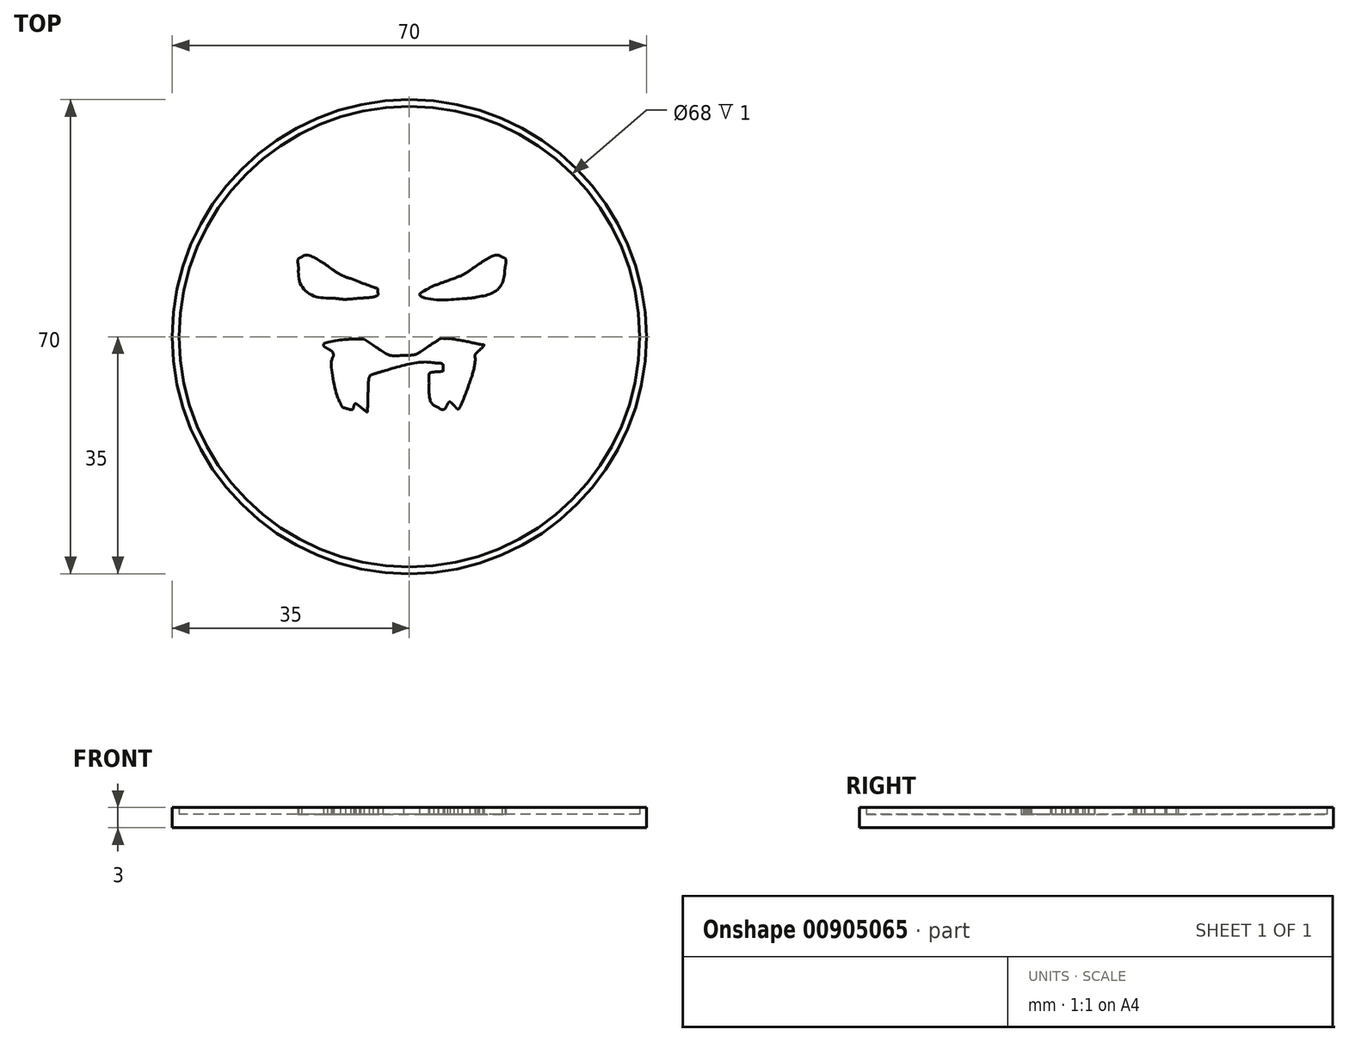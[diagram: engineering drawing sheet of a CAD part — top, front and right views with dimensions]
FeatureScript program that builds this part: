
annotation { "Feature Type Name" : "Feature", "Feature Type Description" : "" }
export const myFeature = defineFeature(function(context is Context, id is Id, definition is map)
    precondition{}
    {
        {
            var Q0;
            Q0=qCreatedBy(makeId("Top.planeOp"),FACE);
            var sketch = newSketch(context, id + "F0", { "sketchPlane" : qUnion([Q0])});
            skLineSegment(sketch, "E0", {"start": v(16.84, 6.63) * mm, "end": v(16.18, 5.27) * mm});
            skLineSegment(sketch, "E1", {"start": v(16.18, 5.27) * mm, "end": v(16.32, 4.06) * mm});
            skLineSegment(sketch, "E2", {"start": v(16.47, -0.82) * mm, "end": v(15.75, -0.73) * mm});
            skLineSegment(sketch, "E3", {"start": v(15.75, -0.73) * mm, "end": v(15.82, -1.4) * mm});
            skLineSegment(sketch, "E4", {"start": v(15.72, -10.07) * mm, "end": v(14.53, -10.08) * mm});
            skLineSegment(sketch, "E5", {"start": v(14.53, -10.08) * mm, "end": v(14.58, -11.4) * mm});
            skLineSegment(sketch, "E6", {"start": v(12.3, -13.5) * mm, "end": v(11.89, -13) * mm});
            skLineSegment(sketch, "E7", {"start": v(11.89, -13) * mm, "end": v(11.47, -13.22) * mm});
            skLineSegment(sketch, "E8", {"start": v(-5.34, 5.77) * mm, "end": v(-6.7, 6.68) * mm});
            skLineSegment(sketch, "E9", {"start": v(-6.7, 6.68) * mm, "end": v(-7.9, 6.65) * mm});
            skFitSpline(sketch, "E10", {"points": [v(0.33, -24.03) * mm, v(-0.4, -23.24) * mm, v(-1.2, -21.92) * mm, v(-1.9, -20.3) * mm]});
            skFitSpline(sketch, "E11", {"points": [v(-1.9, -20.3) * mm, v(-2.2, -19.61) * mm, v(-2.49, -19) * mm, v(-2.55, -18.93) * mm]});
            skFitSpline(sketch, "E12", {"points": [v(-2.55, -18.93) * mm, v(-2.61, -18.87) * mm, v(-2.73, -19.07) * mm, v(-2.8, -19.4) * mm]});
            skFitSpline(sketch, "E13", {"points": [v(-2.8, -19.4) * mm, v(-3.12, -20.6) * mm, v(-3.98, -22.41) * mm, v(-4.25, -22.41) * mm]});
            skFitSpline(sketch, "E14", {"points": [v(-4.25, -22.41) * mm, v(-4.3, -22.41) * mm, v(-4.47, -22.16) * mm, v(-4.6, -21.85) * mm]});
            skFitSpline(sketch, "E15", {"points": [v(-4.6, -21.85) * mm, v(-5.08, -20.8) * mm, v(-7.45, -18.8) * mm, v(-9.5, -17.73) * mm]});
            skFitSpline(sketch, "E16", {"points": [v(-9.5, -17.73) * mm, v(-10.12, -17.41) * mm, v(-10.24, -17.4) * mm, v(-10.66, -17.53) * mm]});
            skFitSpline(sketch, "E17", {"points": [v(-10.66, -17.53) * mm, v(-10.93, -17.62) * mm, v(-11.34, -17.94) * mm, v(-11.65, -18.3) * mm]});
            skFitSpline(sketch, "E18", {"points": [v(-11.65, -18.3) * mm, v(-12.3, -19.05) * mm, v(-12.42, -18.97) * mm, v(-12.62, -17.67) * mm]});
            skFitSpline(sketch, "E19", {"points": [v(-12.62, -17.67) * mm, v(-12.78, -16.65) * mm, v(-12.7, -16.7) * mm, v(-13.62, -16.96) * mm]});
            skFitSpline(sketch, "E20", {"points": [v(-13.62, -16.96) * mm, v(-13.9, -17.04) * mm, v(-13.93, -17.01) * mm, v(-13.84, -16.73) * mm]});
            skFitSpline(sketch, "E21", {"points": [v(-13.84, -16.73) * mm, v(-13.56, -15.8) * mm, v(-13.53, -15.46) * mm, v(-13.65, -14.74) * mm]});
            skFitSpline(sketch, "E22", {"points": [v(-13.65, -14.74) * mm, v(-13.79, -13.85) * mm, v(-14.24, -12.57) * mm, v(-14.45, -12.43) * mm]});
            skFitSpline(sketch, "E23", {"points": [v(-14.45, -12.43) * mm, v(-14.53, -12.38) * mm, v(-14.7, -12.46) * mm, v(-14.8, -12.6) * mm]});
            skFitSpline(sketch, "E24", {"points": [v(-14.8, -12.6) * mm, v(-15.1, -12.95) * mm, v(-15.63, -13.3) * mm, v(-15.87, -13.3) * mm]});
            skFitSpline(sketch, "E25", {"points": [v(-15.87, -13.3) * mm, v(-16.05, -13.3) * mm, v(-16.08, -12.94) * mm, v(-16.09, -10.64) * mm]});
            skFitSpline(sketch, "E26", {"points": [v(-16.09, -10.64) * mm, v(-16.1, -9.17) * mm, v(-16.16, -7.82) * mm, v(-16.23, -7.64) * mm]});
            skFitSpline(sketch, "E27", {"points": [v(-16.23, -7.64) * mm, v(-16.36, -7.33) * mm, v(-16.39, -7.32) * mm, v(-17.7, -7.36) * mm]});
            skFitSpline(sketch, "E28", {"points": [v(-17.7, -7.36) * mm, v(-19.04, -7.4) * mm, v(-19.26, -7.32) * mm, v(-18.83, -6.97) * mm]});
            skFitSpline(sketch, "E29", {"points": [v(-18.83, -6.97) * mm, v(-18.49, -6.68) * mm, v(-17.98, -5.55) * mm, v(-17.75, -4.55) * mm]});
            skFitSpline(sketch, "E30", {"points": [v(-17.75, -4.55) * mm, v(-17.45, -3.23) * mm, v(-17.46, 0.97) * mm, v(-17.77, 3.12) * mm]});
            skFitSpline(sketch, "E31", {"points": [v(-17.77, 3.12) * mm, v(-17.98, 4.54) * mm, v(-18.06, 4.8) * mm, v(-18.59, 5.71) * mm]});
            skFitSpline(sketch, "E32", {"points": [v(-18.59, 5.71) * mm, v(-19.63, 7.52) * mm, v(-20.1, 8.95) * mm, v(-20.1, 10.3) * mm]});
            skFitSpline(sketch, "E33", {"points": [v(-20.1, 10.3) * mm, v(-20.1, 11.28) * mm, v(-19.85, 11.91) * mm, v(-19.13, 12.85) * mm]});
            skFitSpline(sketch, "E34", {"points": [v(-19.13, 12.85) * mm, v(-18.32, 13.92) * mm, v(-18.18, 15.6) * mm, v(-18.78, 17.2) * mm]});
            skFitSpline(sketch, "E35", {"points": [v(-18.78, 17.2) * mm, v(-18.94, 17.63) * mm, v(-19.36, 18.28) * mm, v(-19.83, 18.83) * mm]});
            skFitSpline(sketch, "E36", {"points": [v(-19.83, 18.83) * mm, v(-20.73, 19.86) * mm, v(-21.42, 21.09) * mm, v(-21.75, 22.23) * mm]});
            skFitSpline(sketch, "E37", {"points": [v(-21.75, 22.23) * mm, v(-22.09, 23.4) * mm, v(-21.97, 26.07) * mm, v(-21.5, 27.62) * mm]});
            skFitSpline(sketch, "E38", {"points": [v(-21.5, 27.62) * mm, v(-21.06, 29.09) * mm, v(-19.85, 31.81) * mm, v(-19.64, 31.81) * mm]});
            skFitSpline(sketch, "E39", {"points": [v(-19.64, 31.81) * mm, v(-19.03, 31.81) * mm, v(-17.7, 30.26) * mm, v(-17.45, 29.24) * mm]});
            skFitSpline(sketch, "E40", {"points": [v(-17.45, 29.24) * mm, v(-17.06, 27.73) * mm, v(-16.88, 27.3) * mm, v(-16.29, 26.4) * mm]});
            skFitSpline(sketch, "E41", {"points": [v(-16.29, 26.4) * mm, v(-15.47, 25.16) * mm, v(-13.78, 23.52) * mm, v(-12.83, 23.06) * mm]});
            skFitSpline(sketch, "E42", {"points": [v(-12.83, 23.06) * mm, v(-12.39, 22.84) * mm, v(-11.72, 22.66) * mm, v(-11.06, 22.58) * mm]});
            skFitSpline(sketch, "E43", {"points": [v(-11.06, 22.58) * mm, v(-10.19, 22.47) * mm, v(-9.75, 22.33) * mm, v(-8.55, 21.72) * mm]});
            skFitSpline(sketch, "E44", {"points": [v(-8.55, 21.72) * mm, v(-7.76, 21.32) * mm, v(-6.36, 20.46) * mm, v(-5.45, 19.81) * mm]});
            skFitSpline(sketch, "E45", {"points": [v(-5.45, 19.81) * mm, v(-2.3, 17.56) * mm, v(-1.48, 17.03) * mm, v(-1.14, 17.03) * mm]});
            skFitSpline(sketch, "E46", {"points": [v(-1.14, 17.03) * mm, v(-0.74, 17.03) * mm, v(0.04, 17.5) * mm, v(1.7, 18.72) * mm]});
            skFitSpline(sketch, "E47", {"points": [v(1.7, 18.72) * mm, v(5.41, 21.46) * mm, v(7.07, 22.35) * mm, v(8.88, 22.58) * mm]});
            skFitSpline(sketch, "E48", {"points": [v(8.88, 22.58) * mm, v(9.43, 22.65) * mm, v(10.18, 22.85) * mm, v(10.6, 23.05) * mm]});
            skFitSpline(sketch, "E49", {"points": [v(10.6, 23.05) * mm, v(12.39, 23.9) * mm, v(14.82, 26.94) * mm, v(15.07, 28.67) * mm]});
            skFitSpline(sketch, "E50", {"points": [v(15.07, 28.67) * mm, v(15.26, 29.87) * mm, v(16.74, 31.9) * mm, v(17.36, 31.78) * mm]});
            skFitSpline(sketch, "E51", {"points": [v(17.36, 31.78) * mm, v(17.77, 31.7) * mm, v(19.17, 28.33) * mm, v(19.55, 26.5) * mm]});
            skFitSpline(sketch, "E52", {"points": [v(19.55, 26.5) * mm, v(19.8, 25.32) * mm, v(19.8, 23.23) * mm, v(19.55, 22.27) * mm]});
            skFitSpline(sketch, "E53", {"points": [v(19.55, 22.27) * mm, v(19.26, 21.16) * mm, v(18.67, 20.08) * mm, v(17.75, 18.99) * mm]});
            skFitSpline(sketch, "E54", {"points": [v(17.75, 18.99) * mm, v(16.83, 17.9) * mm, v(16.6, 17.5) * mm, v(16.36, 16.57) * mm]});
            skFitSpline(sketch, "E55", {"points": [v(16.36, 16.57) * mm, v(16, 15.18) * mm, v(16.24, 13.67) * mm, v(17, 12.73) * mm]});
            skFitSpline(sketch, "E56", {"points": [v(17, 12.73) * mm, v(18.26, 11.16) * mm, v(18.22, 9.49) * mm, v(16.84, 6.63) * mm]});
            skFitSpline(sketch, "E57", {"points": [v(16.32, 4.06) * mm, v(16.54, 2.03) * mm, v(16.85, 0.43) * mm, v(17.17, -0.32) * mm]});
            skFitSpline(sketch, "E58", {"points": [v(17.17, -0.32) * mm, v(17.27, -0.56) * mm, v(17.31, -0.79) * mm, v(17.27, -0.83) * mm]});
            skFitSpline(sketch, "E59", {"points": [v(17.27, -0.83) * mm, v(17.23, -0.87) * mm, v(16.87, -0.87) * mm, v(16.47, -0.82) * mm]});
            skFitSpline(sketch, "E60", {"points": [v(15.82, -1.4) * mm, v(15.93, -2.32) * mm, v(16.3, -2.98) * mm, v(17.38, -4.21) * mm]});
            skFitSpline(sketch, "E61", {"points": [v(17.38, -4.21) * mm, v(18.3, -5.26) * mm, v(18.3, -5.26) * mm, v(17.99, -5.4) * mm]});
            skFitSpline(sketch, "E62", {"points": [v(17.99, -5.4) * mm, v(17.74, -5.52) * mm, v(17.5, -5.5) * mm, v(16.96, -5.35) * mm]});
            skFitSpline(sketch, "E63", {"points": [v(16.96, -5.35) * mm, v(16.57, -5.23) * mm, v(16.2, -5.19) * mm, v(16.15, -5.24) * mm]});
            skFitSpline(sketch, "E64", {"points": [v(16.15, -5.24) * mm, v(15.8, -5.6) * mm, v(16.77, -7.73) * mm, v(17.73, -8.72) * mm]});
            skFitSpline(sketch, "E65", {"points": [v(17.73, -8.72) * mm, v(18.15, -9.15) * mm, v(18.18, -9.23) * mm, v(18.02, -9.43) * mm]});
            skFitSpline(sketch, "E66", {"points": [v(18.02, -9.43) * mm, v(17.67, -9.85) * mm, v(16.95, -10.05) * mm, v(15.72, -10.07) * mm]});
            skFitSpline(sketch, "E67", {"points": [v(14.58, -11.4) * mm, v(14.6, -12.3) * mm, v(14.56, -12.97) * mm, v(14.42, -13.52) * mm]});
            skFitSpline(sketch, "E68", {"points": [v(14.42, -13.52) * mm, v(14.18, -14.43) * mm, v(13.68, -15.68) * mm, v(13.56, -15.68) * mm]});
            skFitSpline(sketch, "E69", {"points": [v(13.56, -15.68) * mm, v(13.5, -15.68) * mm, v(13.3, -15.3) * mm, v(13.1, -14.84) * mm]});
            skFitSpline(sketch, "E70", {"points": [v(13.1, -14.84) * mm, v(12.9, -14.37) * mm, v(12.54, -13.77) * mm, v(12.3, -13.5) * mm]});
            skFitSpline(sketch, "E71", {"points": [v(11.47, -13.22) * mm, v(10.74, -13.6) * mm, v(9.51, -14.85) * mm, v(9.1, -15.64) * mm]});
            skFitSpline(sketch, "E72", {"points": [v(9.1, -15.64) * mm, v(8.87, -16.07) * mm, v(8.56, -16.91) * mm, v(8.4, -17.53) * mm]});
            skFitSpline(sketch, "E73", {"points": [v(8.4, -17.53) * mm, v(8.05, -19) * mm, v(7.59, -19.88) * mm, v(6.68, -20.86) * mm]});
            skFitSpline(sketch, "E74", {"points": [v(6.68, -20.86) * mm, v(5.89, -21.73) * mm, v(5.63, -21.77) * mm, v(5.63, -21.04) * mm]});
            skFitSpline(sketch, "E75", {"points": [v(5.63, -21.04) * mm, v(5.63, -20.56) * mm, v(4.88, -18.96) * mm, v(4.44, -18.49) * mm]});
            skFitSpline(sketch, "E76", {"points": [v(4.44, -18.49) * mm, v(4.22, -18.24) * mm, v(4.11, -18.21) * mm, v(3.9, -18.33) * mm]});
            skFitSpline(sketch, "E77", {"points": [v(3.9, -18.33) * mm, v(3.17, -18.72) * mm, v(2.35, -20.5) * mm, v(1.7, -23.1) * mm]});
            skFitSpline(sketch, "E78", {"points": [v(1.7, -23.1) * mm, v(1.44, -24.09) * mm, v(1.25, -24.6) * mm, v(1.12, -24.63) * mm]});
            skFitSpline(sketch, "E79", {"points": [v(1.12, -24.63) * mm, v(1.01, -24.65) * mm, v(0.66, -24.38) * mm, v(0.33, -24.03) * mm]});
            skFitSpline(sketch, "E80", {"points": [v(-6.1, -1.5) * mm, v(-6.06, -0.27) * mm, v(-5.98, 0.84) * mm, v(-5.92, 0.96) * mm]});
            skFitSpline(sketch, "E81", {"points": [v(-5.92, 0.96) * mm, v(-5.8, 1.25) * mm, v(-5.24, 1.51) * mm, v(-3.87, 1.9) * mm]});
            skFitSpline(sketch, "E82", {"points": [v(-3.87, 1.9) * mm, v(-0.9, 2.77) * mm, v(2.08, 3.26) * mm, v(3.62, 3.14) * mm]});
            skFitSpline(sketch, "E83", {"points": [v(3.62, 3.14) * mm, v(4.74, 3.06) * mm, v(4.97, 2.92) * mm, v(4.97, 2.33) * mm]});
            skFitSpline(sketch, "E84", {"points": [v(4.97, 2.33) * mm, v(4.97, 1.9) * mm, v(4.96, 1.9) * mm, v(4.22, 1.82) * mm]});
            skFitSpline(sketch, "E85", {"points": [v(4.22, 1.82) * mm, v(3.12, 1.7) * mm, v(2.92, 1.46) * mm, v(2.93, 0.18) * mm]});
            skFitSpline(sketch, "E86", {"points": [v(2.93, 0.18) * mm, v(2.95, -1.77) * mm, v(3.39, -2.93) * mm, v(4.29, -3.46) * mm]});
            skFitSpline(sketch, "E87", {"points": [v(4.29, -3.46) * mm, v(4.82, -3.77) * mm, v(5.26, -3.62) * mm, v(5.6, -3.02) * mm]});
            skFitSpline(sketch, "E88", {"points": [v(5.6, -3.02) * mm, v(5.73, -2.8) * mm, v(5.9, -2.62) * mm, v(5.98, -2.62) * mm]});
            skFitSpline(sketch, "E89", {"points": [v(5.98, -2.62) * mm, v(6.06, -2.62) * mm, v(6.34, -2.86) * mm, v(6.6, -3.15) * mm]});
            skFitSpline(sketch, "E90", {"points": [v(6.6, -3.15) * mm, v(6.86, -3.44) * mm, v(7.12, -3.68) * mm, v(7.18, -3.68) * mm]});
            skFitSpline(sketch, "E91", {"points": [v(7.18, -3.68) * mm, v(7.29, -3.68) * mm, v(8.5, -0.89) * mm, v(8.94, 0.37) * mm]});
            skFitSpline(sketch, "E92", {"points": [v(8.94, 0.37) * mm, v(9.3, 1.41) * mm, v(9.71, 3.27) * mm, v(9.72, 3.9) * mm]});
            skFitSpline(sketch, "E93", {"points": [v(9.72, 3.9) * mm, v(9.72, 4.34) * mm, v(9.8, 4.5) * mm, v(10.31, 4.98) * mm]});
            skFitSpline(sketch, "E94", {"points": [v(10.31, 4.98) * mm, v(10.86, 5.51) * mm, v(11.05, 5.82) * mm, v(10.8, 5.82) * mm]});
            skFitSpline(sketch, "E95", {"points": [v(10.8, 5.82) * mm, v(10.75, 5.82) * mm, v(10.26, 5.91) * mm, v(9.72, 6.03) * mm]});
            skFitSpline(sketch, "E96", {"points": [v(9.72, 6.03) * mm, v(7.88, 6.42) * mm, v(5.83, 6.74) * mm, v(5.21, 6.74) * mm]});
            skFitSpline(sketch, "E97", {"points": [v(5.21, 6.74) * mm, v(4.69, 6.74) * mm, v(4.43, 6.63) * mm, v(3.37, 5.93) * mm]});
            skFitSpline(sketch, "E98", {"points": [v(3.37, 5.93) * mm, v(1.35, 4.6) * mm, v(0.64, 4.32) * mm, v(-0.84, 4.26) * mm]});
            skFitSpline(sketch, "E99", {"points": [v(-0.84, 4.26) * mm, v(-2.49, 4.2) * mm, v(-3.46, 4.52) * mm, v(-5.34, 5.77) * mm]});
            skFitSpline(sketch, "E100", {"points": [v(-7.9, 6.65) * mm, v(-9.17, 6.62) * mm, v(-12.6, 5.97) * mm, v(-12.66, 5.75) * mm]});
            skFitSpline(sketch, "E101", {"points": [v(-12.66, 5.75) * mm, v(-12.68, 5.68) * mm, v(-12.43, 5.46) * mm, v(-12.1, 5.26) * mm]});
            skFitSpline(sketch, "E102", {"points": [v(-12.1, 5.26) * mm, v(-11.5, 4.9) * mm, v(-11.2, 4.38) * mm, v(-11.3, 3.94) * mm]});
            skFitSpline(sketch, "E103", {"points": [v(-11.3, 3.94) * mm, v(-11.51, 3.15) * mm, v(-10.75, -1.45) * mm, v(-10.2, -2.73) * mm]});
            skFitSpline(sketch, "E104", {"points": [v(-10.2, -2.73) * mm, v(-9.95, -3.3) * mm, v(-9.83, -3.43) * mm, v(-9.43, -3.54) * mm]});
            skFitSpline(sketch, "E105", {"points": [v(-9.43, -3.54) * mm, v(-8.6, -3.77) * mm, v(-8.36, -3.72) * mm, v(-8.2, -3.28) * mm]});
            skFitSpline(sketch, "E106", {"points": [v(-8.2, -3.28) * mm, v(-8.13, -3.06) * mm, v(-8.01, -2.89) * mm, v(-7.95, -2.89) * mm]});
            skFitSpline(sketch, "E107", {"points": [v(-7.95, -2.89) * mm, v(-7.88, -2.89) * mm, v(-7.55, -3.1) * mm, v(-7.22, -3.35) * mm]});
            skFitSpline(sketch, "E108", {"points": [v(-7.22, -3.35) * mm, v(-6.21, -4.12) * mm, v(-6.2, -4.08) * mm, v(-6.1, -1.5) * mm]});
            skFitSpline(sketch, "E109", {"points": [v(-7.39, 12.68) * mm, v(-5.6, 12.83) * mm, v(-4.66, 13.15) * mm, v(-4.66, 13.6) * mm]});
            skFitSpline(sketch, "E110", {"points": [v(-4.66, 13.6) * mm, v(-4.66, 14.05) * mm, v(-5.07, 14.25) * mm, v(-8.69, 15.58) * mm]});
            skFitSpline(sketch, "E111", {"points": [v(-8.69, 15.58) * mm, v(-9.69, 15.95) * mm, v(-10.53, 16.38) * mm, v(-11.4, 16.97) * mm]});
            skFitSpline(sketch, "E112", {"points": [v(-11.4, 16.97) * mm, v(-13.52, 18.4) * mm, v(-15.21, 19.06) * mm, v(-15.93, 18.73) * mm]});
            skFitSpline(sketch, "E113", {"points": [v(-15.93, 18.73) * mm, v(-16.34, 18.54) * mm, v(-16.46, 18.15) * mm, v(-16.36, 17.32) * mm]});
            skFitSpline(sketch, "E114", {"points": [v(-16.36, 17.32) * mm, v(-16.06, 14.77) * mm, v(-14.1, 13.03) * mm, v(-11.16, 12.69) * mm]});
            skFitSpline(sketch, "E115", {"points": [v(-11.16, 12.69) * mm, v(-9.87, 12.54) * mm, v(-9.15, 12.54) * mm, v(-7.39, 12.68) * mm]});
            skFitSpline(sketch, "E116", {"points": [v(10.07, 12.9) * mm, v(12.3, 13.47) * mm, v(13.74, 14.97) * mm, v(14.11, 17.1) * mm]});
            skFitSpline(sketch, "E117", {"points": [v(14.11, 17.1) * mm, v(14.28, 18.12) * mm, v(14.18, 18.54) * mm, v(13.7, 18.74) * mm]});
            skFitSpline(sketch, "E118", {"points": [v(13.7, 18.74) * mm, v(12.93, 19.06) * mm, v(11.45, 18.47) * mm, v(9.17, 16.95) * mm]});
            skFitSpline(sketch, "E119", {"points": [v(9.17, 16.95) * mm, v(8.12, 16.25) * mm, v(7.46, 15.94) * mm, v(5.55, 15.24) * mm]});
            skFitSpline(sketch, "E120", {"points": [v(5.55, 15.24) * mm, v(4.27, 14.77) * mm, v(3.05, 14.27) * mm, v(2.84, 14.12) * mm]});
            skFitSpline(sketch, "E121", {"points": [v(2.84, 14.12) * mm, v(1.52, 13.18) * mm, v(3.88, 12.47) * mm, v(7.78, 12.63) * mm]});
            skFitSpline(sketch, "E122", {"points": [v(7.78, 12.63) * mm, v(8.63, 12.67) * mm, v(9.66, 12.78) * mm, v(10.07, 12.9) * mm]});
            skSolve(sketch);
        }
        {
            var Q0;
            Q0 = qSketchRegion(id + "F0", true);
            extrude(context, id + "F1", {"entities" : qUnion([Q0]), "depth" : 1 * mm, "offsetDistance" : 25 * mm});
        }
        {
            var Q0;
            Q0=qCreatedBy(makeId("Top.planeOp"),FACE);
            var sketch = newSketch(context, id + "F2", { "sketchPlane" : qUnion([Q0])});
            skCircle(sketch, "E123", {"center": v(0, 7) * mm, "radius": 35 * mm});
            skSolve(sketch);
        }
        {
            var Q0;
            Q0=makeQuery(id+"F2.imprint","IMPRINT",FACE,{"disambiguationData":[TD([[makeQuery(id+"F2.imprint","IMPRINT",EDGE,{"derivedFrom":sQuery(id+"F2.wireOp",EDGE,"E123")}),1.0]])]});
            extrude(context, id + "F3", {"entities" : qUnion([Q0]), "oppositeDirection" : true, "depth" : 2 * mm, "offsetDistance" : 25 * mm});
        }
        {
            var Q0;
            Q0=makeQuery(id+"F3.opExtrude","CAP_FACE",FACE,{"disambiguationData":[OSD([sQuery(id+"F2.wireOp",EDGE,"E123")])],"isStart":true});
            var sketch = newSketch(context, id + "F4", { "sketchPlane" : qUnion([Q0])});
            skCircle(sketch, "E124", {"center": v(0, 7) * mm, "radius": 34 * mm});
            skCircle(sketch, "E125.0", {"center": v(0, 7) * mm, "radius": 35 * mm});
            skSolve(sketch);
        }
        {
            var Q0;
            Q0=makeQuery(id+"F4.imprint","IMPRINT",FACE,{"disambiguationData":[TD([[makeQuery(id+"F4.imprint","IMPRINT",EDGE,{"derivedFrom":sQuery(id+"F4.wireOp",EDGE,"E124")}),-1.0]])]});
            extrude(context, id + "F5", {"entities" : qUnion([Q0]), "operationType" : NewBodyOperationType.ADD, "depth" : 1 * mm, "offsetDistance" : 25 * mm});
        }
    });
